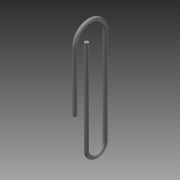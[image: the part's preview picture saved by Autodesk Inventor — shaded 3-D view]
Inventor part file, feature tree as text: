
AUTODESK INVENTOR PART (.ipt)
format: ipt  version: 2015 (Build 190159000, 159)  size: 96,768 bytes
history: native  units: in
note: dims shown in document units (in); Inventor stores cm internally (conversion verified against a paired STEP export)
features: sketch x2, sweep x1
ambient origin geometry x8: Origin, YZ Plane, XZ Plane, XY Plane, X Axis, Y Axis, Z Axis, Center Point
bodies: Solid1 (feature_tree)
feature tree (3):
  sweep  "Sweep1"
  sketch  "Sketch7"  dims[d2=0.01in d3=0.0in d4=0.0in]
  sketch  "Sketch8"
